# Revit family: IS_ConnectSpace_E1186_BIM_FR
name_source: partatom
category: Plumbing Fixtures
revit_build: Autodesk Revit 2017 (Build: 20160225_1515(x64)
units: mm (PartAtom-declared; Revit-internal decimal feet)

## family parameters
Always vertical = No
Cut with Voids When Loaded = No
OmniClass Number = 23.45.05.21.11.11
OmniClass Title = Water Operated Water Closets
Part Type = Normal
Room Calculation Point = No
Round Connector Dimension = Use Diameter
Shared = No
Work Plane-Based = No

## types (1)
- E118601 - CONNECT S C/C BWL HO WHITE BTW
    Accessoires = www.idealspec.fr
    Auteur = Ideal Standard
    BIMobject category = Toilets
    BIMobject category code = sanitary-toilets
    BIMobject main category = Sanitary
    BIMobject main category code = sanitary
    BOSUseNativeGeometries = 1
    Bim-NomDuProjet = ISI_IdealStandard_WcPans_CONNECT_E118601
    Brand url = www.idealspec.fr
    Caractéristiques = CONNECT SPACE CC HO BTW CONNECT SPACE SHORT PROJECTION BOWL [MM] UP TO BLOCK MOULD
    Conformité = NF
    ConseilsDInstallation = 0
    Cost = 0 $
    Couleur = Blanc
    CouleurWc = Blanc
    CoûtDeRemplacement = 0
    Date of publishing = 2018_07_24
    DateDeCréation = 2018_07_24
    Description = CONNECT SPACE CC HO BTW CONNECT SPACE SHORT PROJECTION BOWL [MM] UP TO BLOCK MOULD
    Dimensions = 400 x 361 x 600mm
    Edition number = 1
    Espace = Interne
    Finition = Blanc
    Forme = Complexe
    Hauteur = 400 mm
    IFC Classification = Sanitary Terminal
    IfcExportAs = TOILETPAN
    IfcExportType = IfcSanitaryTerminalType
    InformationsProduit = www.idealspec.fr
    Installation instructions = http://www.idealspec.fr
    Largeur = 361 mm
    Longueur = 600 mm
    Manufacturer name = Ideal Standard
    Marque = Ideal Standard
    Material main = Ceramics
    Matériel = Ceramics
    Model = E118601
    NBS Reference Code = 35-93-94
    NBS Reference Description = Wc Pans
    Nominal height = 765
    Nominal width = 365
    Product Guid = f2539ee7-726a-4971-a992-17a37a191beb
    Product SKU = E1186
    Product certification = http://www.idealspec.fr
    Product data url = https://bimobject.com
    Product family = Sanitary
    Product group = WC pans
    Product name = CONNECT SPACE CC HO BTW CONNECT SPACE SHORT PROJECTION BOWL [MM] UP TO BLOCK MOULD
    Profondeur = 0 mm  [stored 0 ft]
    QR code = http://bimobject.com
    Raccordement = Plomberie
    Révision = 1
    Technical description = http://www.idealspec.fr
    TypeDeCuvette = Washdown
    TypeDeWc = Domestic
    URL = www.idealspec.fr
    Uniclass 2.0 Code = PR-35-93-94
    Uniclass 2.0 Description = Wc Pans
    Uniclass 2015 Code = Pr_40_20_93_94
    Uniclass 2015 Name = WC pans
    Uniclass2015Code = Pr_40_20_93_94
    Uniclass2015Title = WC pans
    Uniclass2015Version = Products v1.1
    UnitéDeMesure = Millimètres
    UnitéDeTemps = An
    UnitéMonétaire = €
    UrlDuFabricant = www.idealspec.fr
    Version = 1
    Weight Net (Kg) = 0
    Youtube clip = http://www.idealspec.fr

note: [stored X ft] marks values corroborated as IEEE doubles in the binary element streams (Revit-internal decimal feet)

## geometry (parser evidence)
native form markers: Sweep x4
no freeform markers — native parametric forms only
